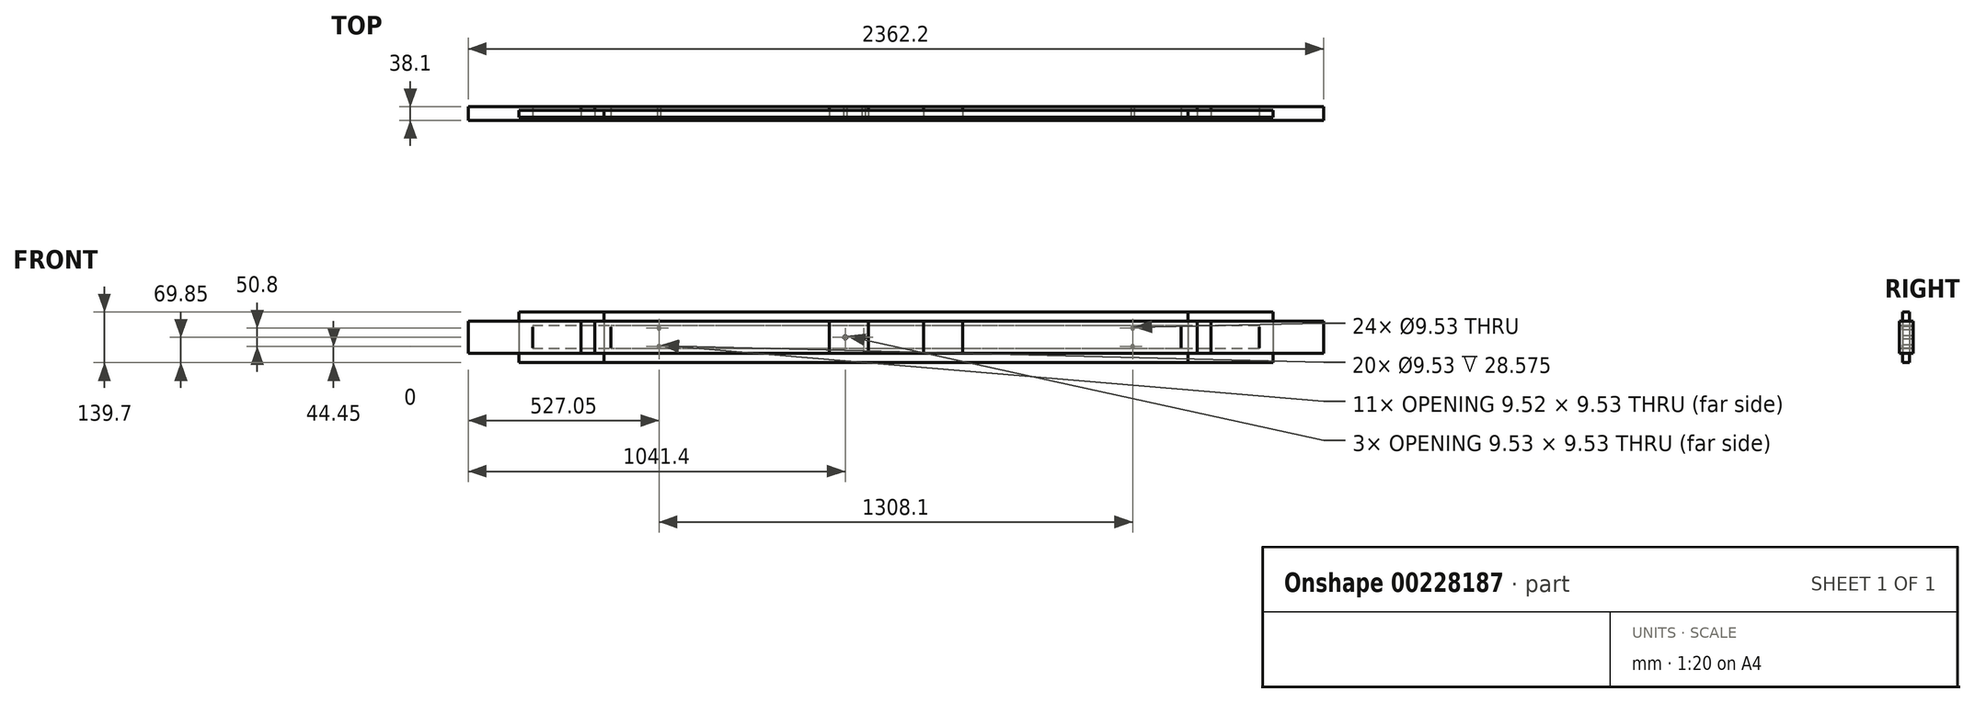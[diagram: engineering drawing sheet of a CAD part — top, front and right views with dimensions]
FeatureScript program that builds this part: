
annotation { "Feature Type Name" : "Feature", "Feature Type Description" : "" }
export const myFeature = defineFeature(function(context is Context, id is Id, definition is map)
    precondition{}
    {
        {
            var Q0;
            Q0=qCreatedBy(makeId("Right.planeOp"),FACE);
            var sketch = newSketch(context, id + "F0", { "sketchPlane" : qUnion([Q0])});
            skLineSegment(sketch, "E0.bottom", {"start": v(15.87, 31.75) * mm, "end": v(-15.88, 31.75) * mm});
            skLineSegment(sketch, "E0.top", {"start": v(15.88, -31.75) * mm, "end": v(-15.87, -31.75) * mm});
            skLineSegment(sketch, "E0.left", {"start": v(19.05, 28.58) * mm, "end": v(19.05, -28.57) * mm});
            skLineSegment(sketch, "E0.right", {"start": v(-19.05, 28.57) * mm, "end": v(-19.05, -28.57) * mm});
            skPoint(sketch, "E0.middle", {"position": v(0, 0) * mm});
            skPoint(sketch, "E1.visualSharp", {"position": v(19.05, 31.75) * mm});
            skArc(sketch, "E1.filletArc", {"start": v(19.05, 28.58) * mm, "mid": v(18.12, 30.82) * mm, "end": v(15.87, 31.75) * mm});
            skPoint(sketch, "E2.visualSharp", {"position": v(-19.05, 31.75) * mm});
            skArc(sketch, "E2.filletArc", {"start": v(-15.88, 31.75) * mm, "mid": v(-18.12, 30.82) * mm, "end": v(-19.05, 28.57) * mm});
            skPoint(sketch, "E3.visualSharp", {"position": v(-19.05, -31.75) * mm});
            skArc(sketch, "E3.filletArc", {"start": v(-19.05, -28.57) * mm, "mid": v(-18.12, -30.82) * mm, "end": v(-15.87, -31.75) * mm});
            skPoint(sketch, "E4.visualSharp", {"position": v(19.05, -31.75) * mm});
            skArc(sketch, "E4.filletArc", {"start": v(15.88, -31.75) * mm, "mid": v(18.12, -30.82) * mm, "end": v(19.05, -28.57) * mm});
            skSolve(sketch);
        }
        {
            var Q0;
            Q0 = qSketchRegion(id + "F0", true);
            extrude(context, id + "F1", {"entities" : qUnion([Q0]), "endBound" : BoundingType.SYMMETRIC, "depth" : 1574.8 * mm});
        }
        {
            var Q0;
            Q0 = qSketchRegion(id + "F0", true);
            extrude(context, id + "F2", {"entities" : qUnion([Q0]), "endBound" : BoundingType.SYMMETRIC, "depth" : 2082.8 * mm - 76.2 * mm});
        }
        {
            var Q0;
            Q0=qCreatedBy(makeId("Right.planeOp"),FACE);
            var sketch = newSketch(context, id + "F3", { "sketchPlane" : qUnion([Q0])});
            skLineSegment(sketch, "E5.bottom", {"start": v(9.52, 69.85) * mm, "end": v(-9.53, 69.85) * mm});
            skLineSegment(sketch, "E5.top", {"start": v(9.52, -69.85) * mm, "end": v(-9.53, -69.85) * mm});
            skLineSegment(sketch, "E5.left", {"start": v(9.52, 69.85) * mm, "end": v(9.52, -69.85) * mm});
            skLineSegment(sketch, "E5.right", {"start": v(-9.53, 69.85) * mm, "end": v(-9.53, -69.85) * mm});
            skPoint(sketch, "E5.middle", {"position": v(0, 0) * mm});
            skSolve(sketch);
        }
        {
            var Q0;
            Q0 = qSketchRegion(id + "F3", true);
            extrude(context, id + "F4", {"entities" : qUnion([Q0]), "endBound" : BoundingType.SYMMETRIC, "depth" : 2082.8 * mm});
        }
        {
            var Q0;
            Q0 = qSketchRegion(id + "F3", true);
            extrude(context, id + "F5", {"entities" : qUnion([Q0]), "endBound" : BoundingType.SYMMETRIC, "depth" : 1612.9 * mm});
        }
        {
            var Q0;
            Q0=qCreatedBy(makeId("Right.planeOp"),FACE);
            var sketch = newSketch(context, id + "F6", { "sketchPlane" : qUnion([Q0])});
            skLineSegment(sketch, "E6.bottom", {"start": v(19.05, 44.45) * mm, "end": v(-19.05, 44.45) * mm});
            skLineSegment(sketch, "E6.top", {"start": v(19.05, -44.45) * mm, "end": v(-19.05, -44.45) * mm});
            skLineSegment(sketch, "E6.left", {"start": v(19.05, 44.45) * mm, "end": v(19.05, -44.45) * mm});
            skLineSegment(sketch, "E6.right", {"start": v(-19.05, 44.45) * mm, "end": v(-19.05, -44.45) * mm});
            skPoint(sketch, "E6.middle", {"position": v(0, 0) * mm});
            skPoint(sketch, "E7.visualSharp", {"position": v(19.05, 44.45) * mm});
            skPoint(sketch, "E8.visualSharp", {"position": v(-19.05, 44.45) * mm});
            skArc(sketch, "E8.filletArc", {"start": v(-15.87, 44.45) * mm, "mid": v(-18.12, 43.52) * mm, "end": v(-19.05, 41.28) * mm});
            skPoint(sketch, "E9.visualSharp", {"position": v(-19.05, -44.45) * mm});
            skArc(sketch, "E9.filletArc", {"start": v(-19.05, -41.28) * mm, "mid": v(-18.12, -43.52) * mm, "end": v(-15.87, -44.45) * mm});
            skPoint(sketch, "E10.visualSharp", {"position": v(19.05, -44.45) * mm});
            skArc(sketch, "E10.filletArc", {"start": v(15.88, -44.45) * mm, "mid": v(18.12, -43.52) * mm, "end": v(19.05, -41.28) * mm});
            skSolve(sketch);
        }
        {
            var Q0;
            Q0 = qSketchRegion(id + "F6", true);
            extrude(context, id + "F7", {"entities" : qUnion([Q0]), "endBound" : BoundingType.SYMMETRIC, "depth" : 1739.9 * mm});
        }
        {
            var Q0;
            Q0 = qSketchRegion(id + "F6", true);
            extrude(context, id + "F8", {"entities" : qUnion([Q0]), "endBound" : BoundingType.SYMMETRIC, "depth" : 2362.2 * mm});
        }
        {
            var Q0;
            Q0 = qSketchRegion(id + "F6", true);
            extrude(context, id + "F9", {"entities" : qUnion([Q0]), "endBound" : BoundingType.SYMMETRIC, "depth" : 152.4 * mm});
        }
        {
            var Q0;
            Q0 = qSketchRegion(id + "F6", true);
            extrude(context, id + "F10", {"entities" : qUnion([Q0]), "endBound" : BoundingType.SYMMETRIC, "depth" : 1663.7 * mm});
        }
        {
            var Q0;
            Q0=makeQuery(id+"F5.opExtrude","SWEPT_FACE",FACE,{"disambiguationData":[OSD([sQuery(id+"F3.wireOp",EDGE,"E5.right")])]});
            var sketch = newSketch(context, id + "F11", { "sketchPlane" : qUnion([Q0])});
            skCircle(sketch, "E11", {"center": v(-654.05, -25.4) * mm, "radius": 4.76 * mm});
            skCircle(sketch, "E12.MirrorC", {"center": v(-654.05, 25.4) * mm, "radius": 4.76 * mm});
            skCircle(sketch, "E13.MirrorC", {"center": v(654.05, -25.4) * mm, "radius": 4.76 * mm});
            skCircle(sketch, "E14.MirrorC", {"center": v(654.05, 25.4) * mm, "radius": 4.76 * mm});
            skSolve(sketch);
        }
        {
            var Q0;
            Q0 = qSketchRegion(id + "F11", true);
            extrude(context, id + "F12", {"entities" : qUnion([Q0]), "operationType" : NewBodyOperationType.REMOVE, "endBound" : BoundingType.THROUGH_ALL, "oppositeDirection" : true, "depth" : 25.4 * mm});
        }
        {
            var Q0;
            Q0 = qSketchRegion(id + "F6", true);
            extrude(context, id + "F13", {"entities" : qUnion([Q0]), "endBound" : BoundingType.SYMMETRIC, "depth" : 368.3 * mm});
        }
        {
            var Q0;
            Q0=makeQuery(id+"F13.opExtrude","SWEPT_FACE",FACE,{"disambiguationData":[OSD([sQuery(id+"F6.wireOp",EDGE,"E6.right")])]});
            var sketch = newSketch(context, id + "F14", { "sketchPlane" : qUnion([Q0])});
            skCircle(sketch, "E15", {"center": v(-139.7, 0) * mm, "radius": 4.76 * mm});
            skCircle(sketch, "E16", {"center": v(-88.9, 0) * mm, "radius": 4.76 * mm});
            skSolve(sketch);
        }
        {
            var Q0;
            Q0 = qSketchRegion(id + "F14", true);
            extrude(context, id + "F15", {"entities" : qUnion([Q0]), "operationType" : NewBodyOperationType.REMOVE, "endBound" : BoundingType.THROUGH_ALL, "oppositeDirection" : true, "depth" : 25.4 * mm});
        }
    });
